# Revit family: VLDF-F149xxWS-xxxLPOxxx
name_source: partatom
category: Leuchten
units: mm (PartAtom-declared; Revit-internal decimal feet)

## family parameters
Basisbauteil = Fläche
Beim Laden mit Abzugskörper schneiden = Nein
Bemaßung runder Anschluss = Durchmesser verwenden
Gemeinsam genutzt = Nein
Lichtquelle = Ja
OmniClass-Nummer = 23.80.70.11
OmniClass-Titel = Luminaries for Internal Lighting
Raumberechnungspunkt = Nein
Teiletyp = Normal

## types (4) — shared parameters
Baugruppenkennzeichen = D5020200
Datei für fotometrisches Netz = VLDF-F149xxx_LPO.IES
Emissionsform beim Rendern sichtbar = Nein
Farbfilter = 16777215
Farbtemperaturverschiebung bei Dämpfen der Lampe = <Keine Auswahl>
Hersteller = RIDI Leuchten GmbH
Lampe = LED
Neigungswinkel = 90.00°
Scheinlast = 31 VA
URL = www.ridi.de
Von Breite des Rechtecks ausssenden = 1483 mm  [stored 4.86549 ft]
Von Länge des Rechtecks aussenden = 36 mm  [stored 0.11811 ft]
brand = RIDI
conformity mark = CE
electrical safety class = 1
height = 65 mm  [stored 0.213255 ft]
ingress protection (IP) code = IP20
length = 1488 mm  [stored 4.88189 ft]
nominal frequency = 50-60Hz
nominal voltage = 230
rated input power = 31
voltage type (AC, DC, UC) = AC
weight = 1,9 kg
width = 36 mm  [stored 0.11811 ft]
zero-valued in all types: Vorgabe-Ansicht

## per-type parameters (varying)
| type | Modell |
| VLDF-F149NDWS-470LPO830 | 0522549 |
| VLDF-F149DAWS-470LPO830 | 0532549 |
| VLDF-F149NDWS-500LPO840 | 0522551 |
| VLDF-F149DAWS-500LPO840 | 0532551 |

note: column(s) folded — value = type name in every type: product name

note: [stored X ft] marks values corroborated as IEEE doubles in the binary element streams (Revit-internal decimal feet)
